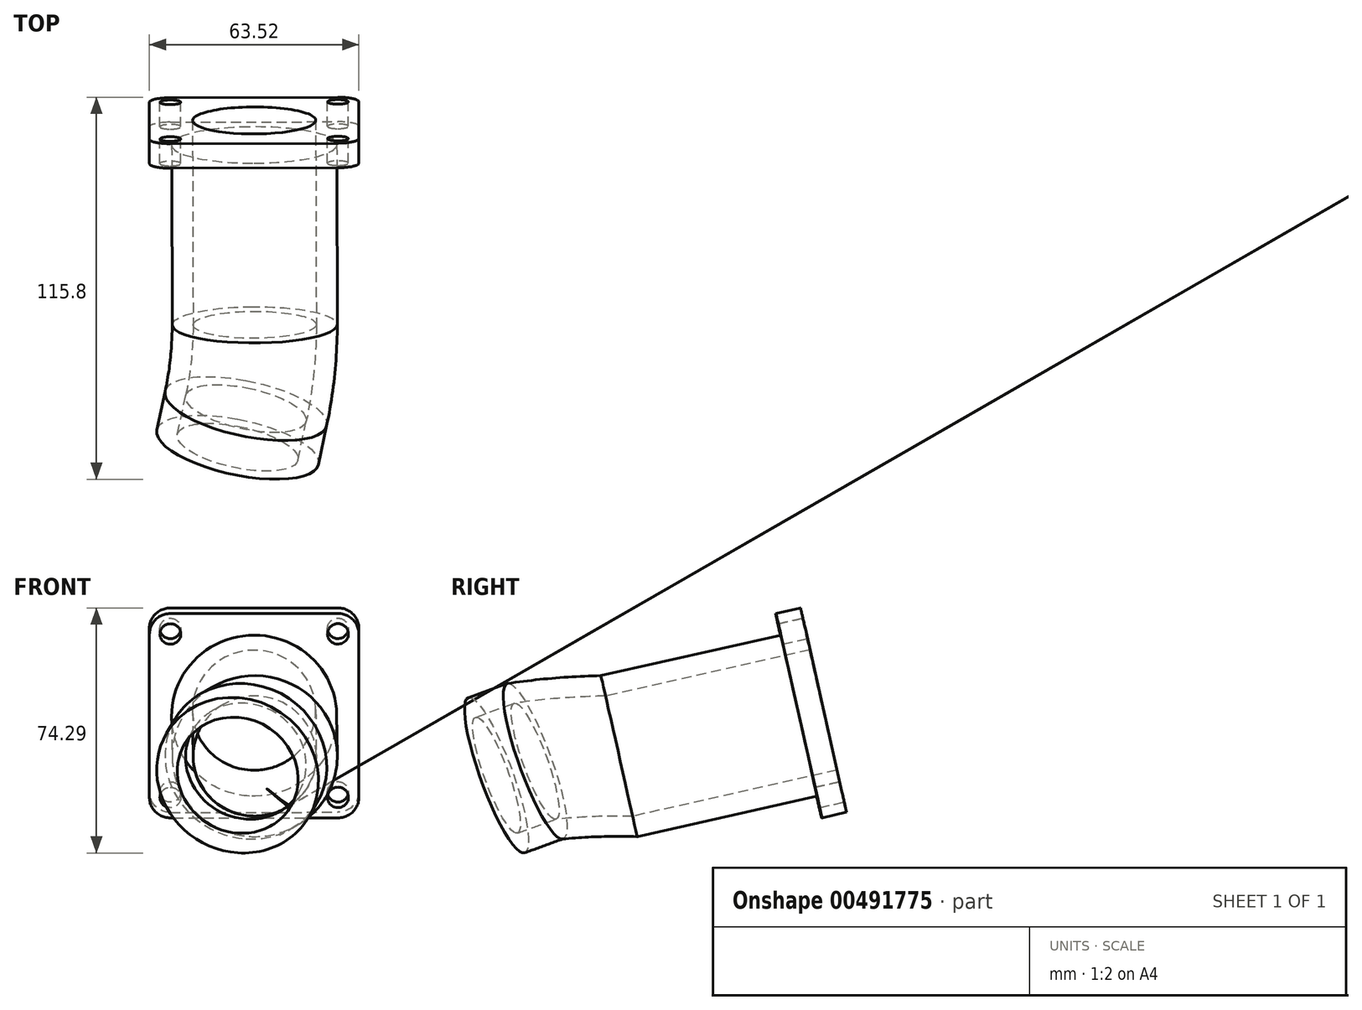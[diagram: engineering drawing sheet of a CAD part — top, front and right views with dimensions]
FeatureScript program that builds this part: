
annotation { "Feature Type Name" : "Feature", "Feature Type Description" : "" }
export const myFeature = defineFeature(function(context is Context, id is Id, definition is map)
    precondition{}
    {
        {
            var Q0;
            Q0=qCreatedBy(makeId("Right.planeOp"),FACE);
            var sketch = newSketch(context, id + "F0", { "sketchPlane" : qUnion([Q0])});
            skLineSegment(sketch, "E0", {"start": v(8.66, -23.88) * mm, "end": v(-8.66, 23.88) * mm, "construction": true});
            skSolve(sketch);
        }
        {
            var Q0;
            Q0=qCreatedBy(makeId("Top.planeOp"),FACE);
            var sketch = newSketch(context, id + "F1", { "sketchPlane" : qUnion([Q0])});
            skLineSegment(sketch, "E1", {"start": v(-24.84, 5.3) * mm, "end": v(24.84, -5.3) * mm, "construction": true});
            skSolve(sketch);
        }
        {
            var Q0;
            Q0=sQuery(id+"F0.wireOp",VERTEX,"E0.end");
            var Q1;
            Q1=sQuery(id+"F1.wireOp",VERTEX,"E1.end");
            var Q2;
            Q2=sQuery(id+"F1.wireOp",VERTEX,"E1.start");
            cPlane(context, id + "F2", {"entities" : qUnion([Q0, Q1, Q2]), "cplaneType" : CPlaneType.THREE_POINT, "offset" : 25.4 * mm, "width" : 152.4 * mm, "height" : 152.4 * mm});
        }
        {
            var Q0;
            Q0=qCreatedBy(makeId("Front.planeOp"),FACE);
            cPlane(context, id + "F3", {"entities" : qUnion([Q0]), "cplaneType" : CPlaneType.OFFSET, "offset" : 25.4 * mm, "oppositeDirection" : true, "width" : 152.4 * mm, "height" : 152.4 * mm});
        }
        {
            var Q0;
            Q0=qCreatedBy(id+"F2.planeOp",FACE);
            var sketch = newSketch(context, id + "F4", { "sketchPlane" : qUnion([Q0])});
            skCircle(sketch, "E2", {"center": v(0, 0) * mm, "radius": 18.67 * mm});
            skCircle(sketch, "E3", {"center": v(0, 0) * mm, "radius": 25.02 * mm});
            skSolve(sketch);
        }
        {
            var Q0;
            Q0=qCreatedBy(makeId("Right.planeOp"),FACE);
            var sketch = newSketch(context, id + "F5", { "sketchPlane" : qUnion([Q0])});
            skLineSegment(sketch, "E4", {"start": v(0, 0) * mm, "end": v(25.4, 9.2) * mm, "construction": true});
            skSolve(sketch);
        }
        {
            var Q0;
            Q0=qCreatedBy(makeId("Top.planeOp"),FACE);
            var sketch = newSketch(context, id + "F6", { "sketchPlane" : qUnion([Q0])});
            skLineSegment(sketch, "E5", {"start": v(0, 0) * mm, "end": v(5.3, 24.84) * mm, "construction": true});
            skSolve(sketch);
        }
        {
            var Q0;
            Q0=qCreatedBy(id+"F3.planeOp",FACE);
            var sketch = newSketch(context, id + "F7", { "sketchPlane" : qUnion([Q0])});
            skLineSegment(sketch, "E6", {"start": v(0, 9.2) * mm, "end": v(5.3, 0) * mm, "construction": true});
            skLineSegment(sketch, "E7", {"start": v(11, 6.33) * mm, "end": v(-11, -6.33) * mm, "construction": true});
            skPoint(sketch, "E8", {"position": v(0, 0) * mm});
            skSolve(sketch);
        }
        {
            var Q0;
            Q0=sQuery(id+"F7.wireOp",EDGE,"E7");
            cPlane(context, id + "F8", {"entities" : qUnion([Q0]), "cplaneType" : CPlaneType.LINE_ANGLE, "offset" : 25.4 * mm, "angle" : 90 * degree, "width" : 152.4 * mm, "height" : 152.4 * mm});
        }
        {
            var Q0;
            Q0=qCreatedBy(id+"F8.planeOp",FACE);
            var sketch = newSketch(context, id + "F9", { "sketchPlane" : qUnion([Q0])});
            skArc(sketch, "E9", {"start": v(0, 0) * mm, "mid": v(2.3, 12.6) * mm, "end": v(3.08, 25.4) * mm});
            skLineSegment(sketch, "E10", {"start": v(3.08, 25.4) * mm, "end": v(3.08, 50.8) * mm, "construction": true});
            skLineSegment(sketch, "E11", {"start": v(0, 0) * mm, "end": v(-103.23, 25.4) * mm, "construction": true});
            skSolve(sketch);
        }
        {
            var Q0;
            Q0=makeQuery(id+"F4.imprint","IMPRINT",FACE,{"disambiguationData":[TD([[makeQuery(id+"F4.imprint","IMPRINT",EDGE,{"derivedFrom":sQuery(id+"F4.wireOp",EDGE,"E2")}),-1.0]])]});
            var Q1;
            Q1=sQuery(id+"F9.wireOp",EDGE,"E9");
            sweep(context, id + "F10", {"profiles" : qUnion([Q0]), "path" : qUnion([Q1])});
        }
        {
            var Q0;
            Q0=makeQuery(id+"F10.opSweep","CAP_FACE",FACE,{"disambiguationData":[OSD([sQuery(id+"F4.wireOp",EDGE,"E2"),sQuery(id+"F4.wireOp",EDGE,"E3"),sQuery(id+"F9.wireOp",VERTEX,"E9.start")])],"isStart":true});
            extrude(context, id + "F11", {"entities" : qUnion([Q0]), "operationType" : NewBodyOperationType.ADD, "depth" : 12.7 * mm});
        }
        {
            var Q0;
            Q0=makeQuery(id+"F10.opSweep","CAP_FACE",FACE,{"disambiguationData":[OSD([sQuery(id+"F4.wireOp",EDGE,"E2"),sQuery(id+"F4.wireOp",EDGE,"E3"),sQuery(id+"F9.wireOp",VERTEX,"E9.end")])],"isStart":false});
            extrude(context, id + "F12", {"entities" : qUnion([Q0]), "operationType" : NewBodyOperationType.ADD, "depth" : 63.5 * mm});
        }
        {
            var Q0;
            Q0=makeQuery(id+"F12.opExtrude","CAP_FACE",FACE,{"disambiguationData":[OSD([sQuery(id+"F4.wireOp",EDGE,"E2"),sQuery(id+"F4.wireOp",EDGE,"E3"),sQuery(id+"F9.wireOp",VERTEX,"E9.end")])],"isStart":false});
            var sketch = newSketch(context, id + "F13", { "sketchPlane" : qUnion([Q0])});
            skLineSegment(sketch, "E12.bottom", {"start": v(22.66, -35.83) * mm, "end": v(-28.14, -35.83) * mm});
            skLineSegment(sketch, "E12.top", {"start": v(22.66, 27.67) * mm, "end": v(-28.14, 27.67) * mm});
            skLineSegment(sketch, "E12.left", {"start": v(29.01, -29.48) * mm, "end": v(29.01, 21.32) * mm});
            skLineSegment(sketch, "E12.right", {"start": v(-34.49, -29.48) * mm, "end": v(-34.49, 21.32) * mm});
            skPoint(sketch, "E12.middle", {"position": v(-2.74, -4.08) * mm});
            skPoint(sketch, "E13.visualSharp", {"position": v(-34.49, 27.67) * mm});
            skArc(sketch, "E13.filletArc", {"start": v(-28.14, 27.67) * mm, "mid": v(-32.63, 25.81) * mm, "end": v(-34.49, 21.32) * mm});
            skPoint(sketch, "E14.visualSharp", {"position": v(29.01, 27.67) * mm});
            skArc(sketch, "E14.filletArc", {"start": v(29.01, 21.32) * mm, "mid": v(27.15, 25.81) * mm, "end": v(22.66, 27.67) * mm});
            skPoint(sketch, "E15.visualSharp", {"position": v(29.01, -35.83) * mm});
            skArc(sketch, "E15.filletArc", {"start": v(22.66, -35.83) * mm, "mid": v(27.15, -33.97) * mm, "end": v(29.01, -29.48) * mm});
            skPoint(sketch, "E16.visualSharp", {"position": v(-34.49, -35.83) * mm});
            skArc(sketch, "E16.filletArc", {"start": v(-34.49, -29.48) * mm, "mid": v(-32.63, -33.97) * mm, "end": v(-28.14, -35.83) * mm});
            skCircle(sketch, "E17", {"center": v(-28.14, 21.32) * mm, "radius": 3.18 * mm});
            skCircle(sketch, "E18", {"center": v(22.66, 21.32) * mm, "radius": 3.18 * mm});
            skCircle(sketch, "E19", {"center": v(22.66, -29.48) * mm, "radius": 3.18 * mm});
            skCircle(sketch, "E20", {"center": v(-28.14, -29.48) * mm, "radius": 3.18 * mm});
            skCircle(sketch, "E21", {"center": v(-2.74, -4.08) * mm, "radius": 18.67 * mm});
            skSolve(sketch);
        }
        {
            var Q0;
            Q0=makeQuery(id+"F13.imprint","IMPRINT",FACE,{"disambiguationData":[TD([[makeQuery(id+"F13.imprint","IMPRINT",EDGE,{"derivedFrom":sQuery(id+"F13.wireOp",EDGE,"E12.bottom")}),-1.0]])]});
            extrude(context, id + "F14", {"entities" : qUnion([Q0]), "operationType" : NewBodyOperationType.ADD, "oppositeDirection" : true, "depth" : 7.62 * mm});
        }
    });
